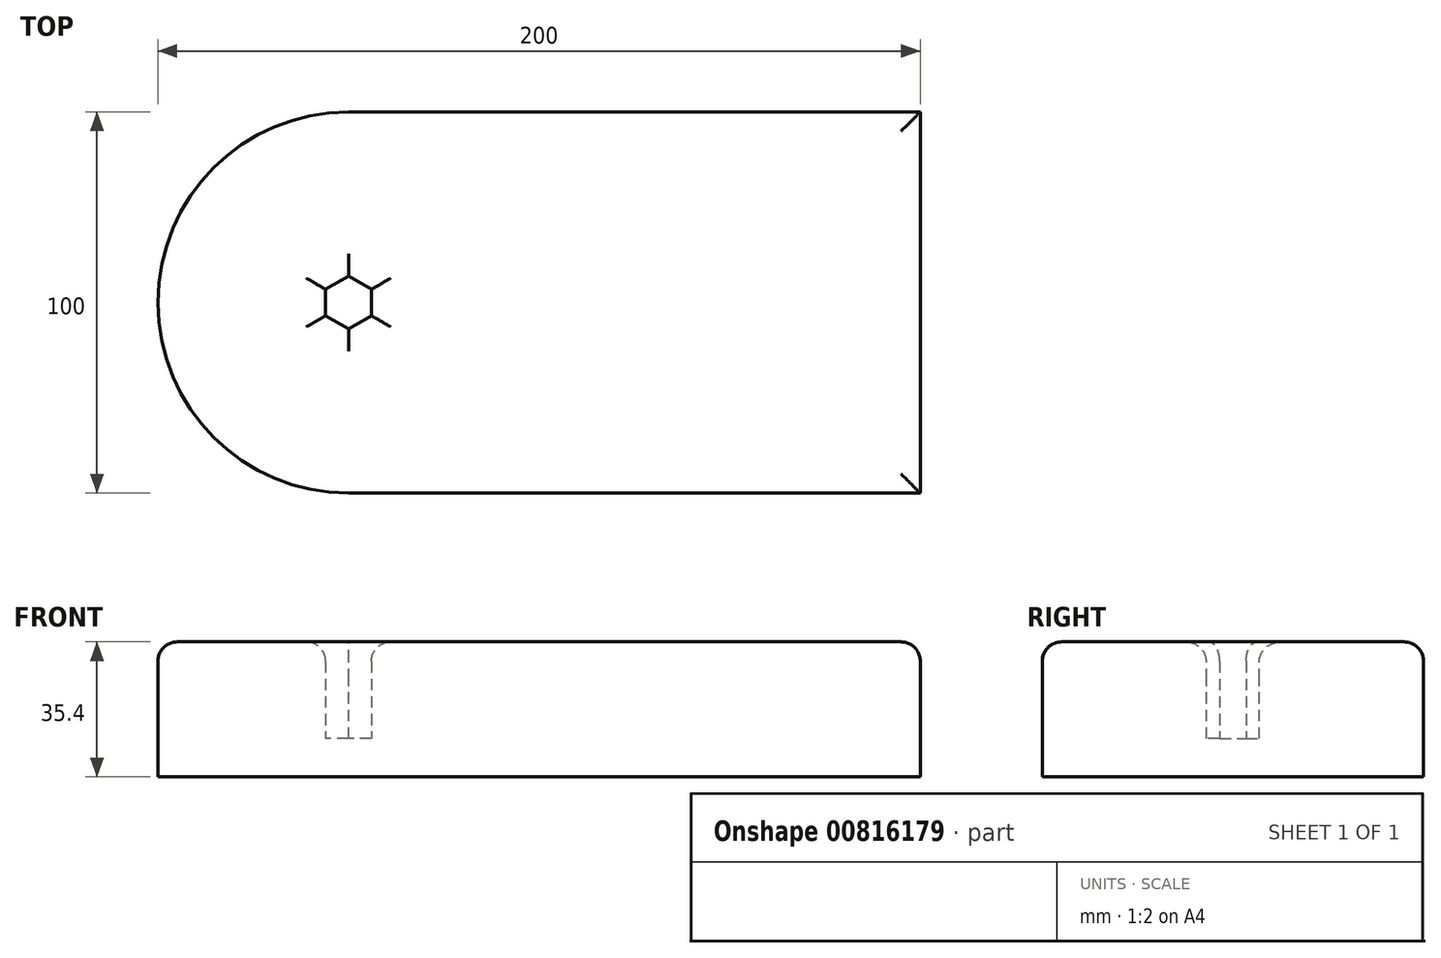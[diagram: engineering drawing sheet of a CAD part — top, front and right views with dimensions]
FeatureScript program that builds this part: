
annotation { "Feature Type Name" : "Feature", "Feature Type Description" : "" }
export const myFeature = defineFeature(function(context is Context, id is Id, definition is map)
    precondition{}
    {
        {
            var Q0;
            Q0=qCreatedBy(makeId("Top.planeOp"),FACE);
            var sketch = newSketch(context, id + "F0", { "sketchPlane" : qUnion([Q0])});
            skLineSegment(sketch, "E0.bottom", {"start": v(-75, -50) * mm, "end": v(75, -50) * mm});
            skLineSegment(sketch, "E0.top", {"start": v(-75, 50) * mm, "end": v(75, 50) * mm});
            skLineSegment(sketch, "E0.left", {"start": v(-75, -50) * mm, "end": v(-75, 50) * mm});
            skLineSegment(sketch, "E0.right", {"start": v(75, -50) * mm, "end": v(75, 50) * mm});
            skPoint(sketch, "E0.middle", {"position": v(0, 0) * mm});
            skSolve(sketch);
        }
        {
            var Q0;
            Q0=makeQuery(id+"F0.imprint","IMPRINT",FACE,{"disambiguationData":[TD([[makeQuery(id+"F0.imprint","IMPRINT",EDGE,{"derivedFrom":sQuery(id+"F0.wireOp",EDGE,"E0.bottom")}),1.0]])]});
            var sketch = newSketch(context, id + "F1", { "sketchPlane" : qUnion([Q0])});
            skCircle(sketch, "E1", {"center": v(-75, 0) * mm, "radius": 50 * mm});
            skCircle(sketch, "E2.cCircle", {"center": v(-75, 0) * mm, "radius": 6 * mm, "construction": true});
            skLineSegment(sketch, "E2.0", {"start": v(-69, 3.46) * mm, "end": v(-69, -3.46) * mm});
            skLineSegment(sketch, "E2.1", {"start": v(-69, -3.46) * mm, "end": v(-75, -6.93) * mm});
            skLineSegment(sketch, "E2.2", {"start": v(-75, -6.93) * mm, "end": v(-81, -3.46) * mm});
            skLineSegment(sketch, "E2.3", {"start": v(-81, -3.46) * mm, "end": v(-81, 3.46) * mm});
            skLineSegment(sketch, "E2.4", {"start": v(-81, 3.46) * mm, "end": v(-75, 6.93) * mm});
            skLineSegment(sketch, "E2.5", {"start": v(-75, 6.93) * mm, "end": v(-69, 3.46) * mm});
            skPoint(sketch, "E2.0.midPoint", {"position": v(-69, 0) * mm});
            skSolve(sketch);
        }
        {
            var Q0;
            Q0=makeQuery(id+"F1.imprint","IMPRINT",FACE,{"disambiguationData":[TD([[makeQuery(id+"F1.imprint","IMPRINT",EDGE,{"derivedFrom":sQuery(id+"F1.wireOp",EDGE,"E2.0")}),1.0]])]});
            var Q1;
            {var subQ1=sQuery(id+"F1.wireOp",EDGE,"E2.2");Q1=makeQuery(id+"F1.imprint","IMPRINT",FACE,{"disambiguationData":[TD([[makeQuery(id+"F1.imprint","IMPRINT",EDGE,{"derivedFrom":subQ1}),1.0]])]});}
            var Q2;
            {var subQ2=makeQuery(id+"F0.imprint","IMPRINT",EDGE,{"derivedFrom":sQuery(id+"F0.wireOp",EDGE,"E0.bottom")});Q2=makeQuery(id+"F1.imprint","IMPRINT",FACE,{"disambiguationData":[TD([[makeQuery(id+"F1.imprint","IMPRINT",EDGE,{"derivedFrom":subQ2}),1.0]])]});}
            extrude(context, id + "F2", {"entities" : qUnion([Q0, Q1, Q2]), "depth" : 25.4 * mm, "offsetDistance" : 25.4 * mm});
        }
        {
            var Q0;
            Q0=makeQuery(id+"F1.imprint","IMPRINT",FACE,{"disambiguationData":[TD([[makeQuery(id+"F1.imprint","IMPRINT",EDGE,{"derivedFrom":sQuery(id+"F1.wireOp",EDGE,"E2.0")}),-1.0]])]});
            var Q1;
            {var subQ0=sQuery(id+"F1.wireOp",EDGE,"E2.2");Q1=makeQuery(id+"F1.imprint","IMPRINT",FACE,{"disambiguationData":[TD([[makeQuery(id+"F1.imprint","IMPRINT",EDGE,{"derivedFrom":subQ0}),-1.0]])]});}
            var Q2;
            Q2=makeQuery(id+"F2.opExtrude","CAP_FACE",FACE,{"disambiguationData":[OSD([sQuery(id+"F0.wireOp",EDGE,"E0.bottom"),sQuery(id+"F0.wireOp",EDGE,"E0.top"),sQuery(id+"F0.wireOp",EDGE,"E0.right"),sQuery(id+"F1.wireOp",EDGE,"E1"),sQuery(id+"F1.wireOp",EDGE,"E2.0"),sQuery(id+"F1.wireOp",EDGE,"E2.1"),sQuery(id+"F1.wireOp",EDGE,"E2.2"),sQuery(id+"F1.wireOp",EDGE,"E2.3"),sQuery(id+"F1.wireOp",EDGE,"E2.4"),sQuery(id+"F1.wireOp",EDGE,"E2.5")])],"isStart":false});
            extrude(context, id + "F3", {"entities" : qUnion([Q0, Q1, Q2]), "operationType" : NewBodyOperationType.ADD, "depth" : 10 * mm, "offsetDistance" : 25.4 * mm});
        }
        {
            var Q0;
            Q0=makeQuery(id+"F3.opExtrude","CAP_FACE",FACE,{"disambiguationData":[OSD([sQuery(id+"F0.wireOp",EDGE,"E0.bottom"),sQuery(id+"F0.wireOp",EDGE,"E0.top"),sQuery(id+"F0.wireOp",EDGE,"E0.right"),sQuery(id+"F1.wireOp",EDGE,"E1"),sQuery(id+"F1.wireOp",EDGE,"E2.0"),sQuery(id+"F1.wireOp",EDGE,"E2.1"),sQuery(id+"F1.wireOp",EDGE,"E2.2"),sQuery(id+"F1.wireOp",EDGE,"E2.3"),sQuery(id+"F1.wireOp",EDGE,"E2.4"),sQuery(id+"F1.wireOp",EDGE,"E2.5")])],"isStart":false});
            var Q1;
            Q1=makeQuery(id+"F3.opExtrude","CAP_EDGE",EDGE,{"disambiguationData":[OSD([sQuery(id+"F1.wireOp",EDGE,"E1")])],"isStart":false});
            fillet(context, id + "F4", {"entities" : qUnion([Q0, Q1]), "radius" : 5.08 * mm, "tangentPropagation" : true, "allowEdgeOverflow" : false});
        }
        {
            var Q0;
            Q0=makeQuery(id+"F3.opExtrude","CAP_FACE",FACE,{"disambiguationData":[OSD([sQuery(id+"F1.wireOp",EDGE,"E2.0"),sQuery(id+"F1.wireOp",EDGE,"E2.1"),sQuery(id+"F1.wireOp",EDGE,"E2.2"),sQuery(id+"F1.wireOp",EDGE,"E2.3"),sQuery(id+"F1.wireOp",EDGE,"E2.4"),sQuery(id+"F1.wireOp",EDGE,"E2.5")])],"isStart":false});
            var sketch = newSketch(context, id + "F5", { "sketchPlane" : qUnion([Q0])});
            skCircle(sketch, "E3", {"center": v(-74.76, 0.4) * mm, "radius": 4 * mm});
            skSolve(sketch);
        }
        {
            var Q0;
            Q0=sQuery(id+"F5.wireOp",EDGE,"E3");
            extrude(context, id + "F6", {"bodyType" : ToolBodyType.SURFACE, "surfaceEntities" : qUnion([Q0]), "depth" : 0 * mm, "offsetDistance" : 25.4 * mm, "hasSecondDirection" : true, "secondDirectionOppositeDirection" : true, "secondDirectionDepth" : 10 * mm});
        }
    });
